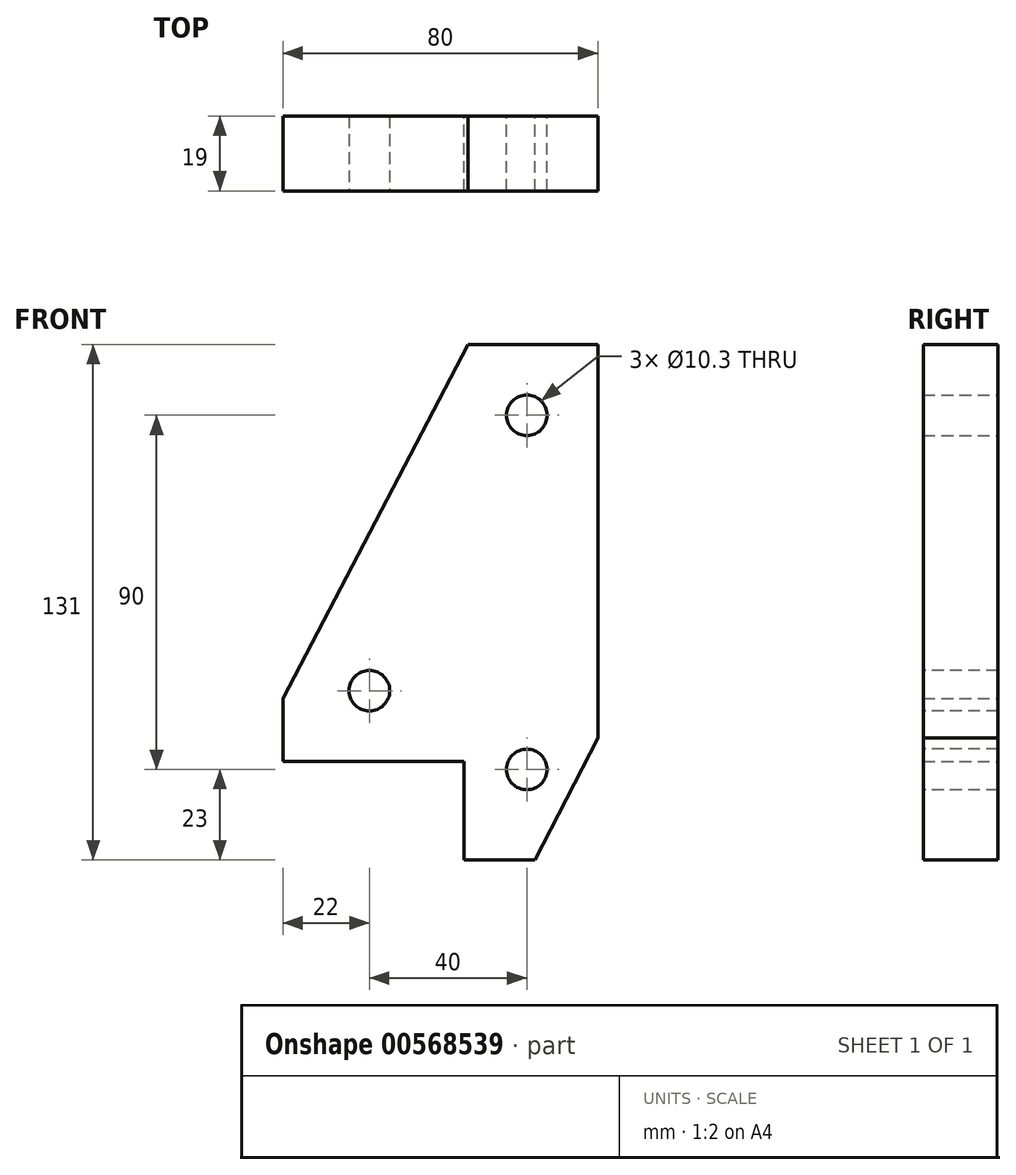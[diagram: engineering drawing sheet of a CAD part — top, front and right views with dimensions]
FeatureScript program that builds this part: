
annotation { "Feature Type Name" : "Feature", "Feature Type Description" : "" }
export const myFeature = defineFeature(function(context is Context, id is Id, definition is map)
    precondition{}
    {
        {
            var Q0;
            Q0=qCreatedBy(makeId("Front.planeOp"),FACE);
            var sketch = newSketch(context, id + "F0", { "sketchPlane" : qUnion([Q0])});
            skLineSegment(sketch, "E0.top", {"start": v(47, 168) * mm, "end": v(80, 168) * mm});
            skLineSegment(sketch, "E0.left", {"start": v(0, 62) * mm, "end": v(0, 78) * mm});
            skLineSegment(sketch, "E0.right", {"start": v(80, 68) * mm, "end": v(80, 168) * mm});
            skPoint(sketch, "E1", {"position": v(80, 68) * mm});
            skPoint(sketch, "E2", {"position": v(45, 0) * mm});
            skPoint(sketch, "E3", {"position": v(0, 78) * mm});
            skPoint(sketch, "E4", {"position": v(47, 168) * mm});
            skPoint(sketch, "E5", {"position": v(62, 150) * mm});
            skPoint(sketch, "E6", {"position": v(22, 47.59) * mm});
            skPoint(sketch, "E7", {"position": v(22, 15) * mm});
            skLineSegment(sketch, "E8", {"start": v(47, 168) * mm, "end": v(0, 78) * mm});
            skLineSegment(sketch, "E9", {"start": v(80, 68) * mm, "end": v(64.04, 37) * mm});
            skPoint(sketch, "E10.orphan", {"position": v(80, 0) * mm});
            skPoint(sketch, "E11", {"position": v(46, 0) * mm});
            skPoint(sketch, "E12", {"position": v(46, 62) * mm});
            skPoint(sketch, "E13", {"position": v(0, 62) * mm});
            skLineSegment(sketch, "E14", {"start": v(46, 62) * mm, "end": v(0, 62) * mm});
            skPoint(sketch, "E15.orphan", {"position": v(0, 0) * mm});
            skPoint(sketch, "E16", {"position": v(46, 37) * mm});
            skLineSegment(sketch, "E17", {"start": v(64.04, 37) * mm, "end": v(46, 37) * mm});
            skLineSegment(sketch, "E18.trimOffspring", {"start": v(46, 37) * mm, "end": v(46, 62) * mm});
            skSolve(sketch);
        }
        {
            var Q0;
            Q0 = qSketchRegion(id + "F0", true);
            var Q1;
            Q1=makeQuery(id+"F0.imprint","IMPRINT",FACE,{"disambiguationData":[TD([[makeQuery(id+"F0.imprint","IMPRINT",EDGE,{"derivedFrom":sQuery(id+"F0.wireOp",EDGE,"E0.top")}),-1.0]])]});
            extrude(context, id + "F1", {"entities" : qUnion([Q0, Q1]), "depth" : 19 * mm, "offsetDistance" : 25 * mm});
        }
        {
            var Q0;
            Q0=sQuery(id+"F0.wireOp",VERTEX,"E5");
            var Q1;
            Q1=makeQuery(id+"F1.opExtrude","SWEPT_BODY",BODY,{"disambiguationData":[OSD([sQuery(id+"F0.wireOp",EDGE,"E0.top"),sQuery(id+"F0.wireOp",EDGE,"E0.left"),sQuery(id+"F0.wireOp",EDGE,"E0.right"),sQuery(id+"F0.wireOp",EDGE,"E8"),sQuery(id+"F0.wireOp",EDGE,"E9"),sQuery(id+"F0.wireOp",EDGE,"9ALEq3iE-AcJ7-wuag-93ND-lzl331uefLuo"),sQuery(id+"F0.wireOp",EDGE,"E14")])]});
            hole(context, id + "F2", {"style" : HoleStyle.SIMPLE, "endStyle" : HoleEndStyle.THROUGH, "oppositeDirection" : true, "standardTappedOrClearance" : lookupTablePath({ "standard" : "ISO", "engagement" : "75%", "pitch" : "1.75 mm", "size" : "M12", "type" : "Tapped" }), "standardBlindInLast" : lookupTablePath({ "standard" : "ISO", "engagement" : "75%", "pitch" : "1.75 mm", "size" : "M12", "type" : "Tapped" }), "holeDiameter" : 10.3 * mm, "showTappedDepth" : true, "isTappedThrough" : true, "tappedDepth" : 8 * mm, "tapClearance" : 3, "startFromSketch" : true, "locations" : qUnion([Q0]), "scope" : qUnion([Q1]), "majorDiameter" : 12 * mm});
        }
        {
            var Q0;
            Q0=makeQuery(id+"F1.opExtrude","CAP_FACE",FACE,{"disambiguationData":[OSD([sQuery(id+"F0.wireOp",EDGE,"E0.top"),sQuery(id+"F0.wireOp",EDGE,"E0.left"),sQuery(id+"F0.wireOp",EDGE,"E0.right"),sQuery(id+"F0.wireOp",EDGE,"E8"),sQuery(id+"F0.wireOp",EDGE,"E9"),sQuery(id+"F0.wireOp",EDGE,"9ALEq3iE-AcJ7-wuag-93ND-lzl331uefLuo"),sQuery(id+"F0.wireOp",EDGE,"E14")])],"isStart":false});
            var sketch = newSketch(context, id + "F3", { "sketchPlane" : qUnion([Q0])});
            skPoint(sketch, "E19", {"position": v(22, 80) * mm});
            skPoint(sketch, "E20", {"position": v(62, 60) * mm});
            skSolve(sketch);
        }
        {
            var Q0;
            Q0=sQuery(id+"F3.wireOp",VERTEX,"E19");
            var Q1;
            Q1=sQuery(id+"F3.wireOp",VERTEX,"E20");
            var Q2;
            Q2=makeQuery(id+"F1.opExtrude","SWEPT_BODY",BODY,{"disambiguationData":[OSD([sQuery(id+"F0.wireOp",EDGE,"E0.top"),sQuery(id+"F0.wireOp",EDGE,"E0.left"),sQuery(id+"F0.wireOp",EDGE,"E0.right"),sQuery(id+"F0.wireOp",EDGE,"E8"),sQuery(id+"F0.wireOp",EDGE,"E9"),sQuery(id+"F0.wireOp",EDGE,"9ALEq3iE-AcJ7-wuag-93ND-lzl331uefLuo"),sQuery(id+"F0.wireOp",EDGE,"E14")])]});
            hole(context, id + "F4", {"style" : HoleStyle.SIMPLE, "endStyle" : HoleEndStyle.THROUGH, "standardTappedOrClearance" : lookupTablePath({ "standard" : "ISO", "engagement" : "75%", "pitch" : "1.75 mm", "size" : "M12", "type" : "Tapped" }), "standardBlindInLast" : lookupTablePath({ "standard" : "ISO", "engagement" : "75%", "pitch" : "1.75 mm", "size" : "M12", "type" : "Tapped" }), "holeDiameter" : 10.3 * mm, "showTappedDepth" : true, "isTappedThrough" : true, "tappedDepth" : 8 * mm, "tapClearance" : 3, "startFromSketch" : true, "locations" : qUnion([Q0, Q1]), "scope" : qUnion([Q2]), "majorDiameter" : 12 * mm});
        }
    });
